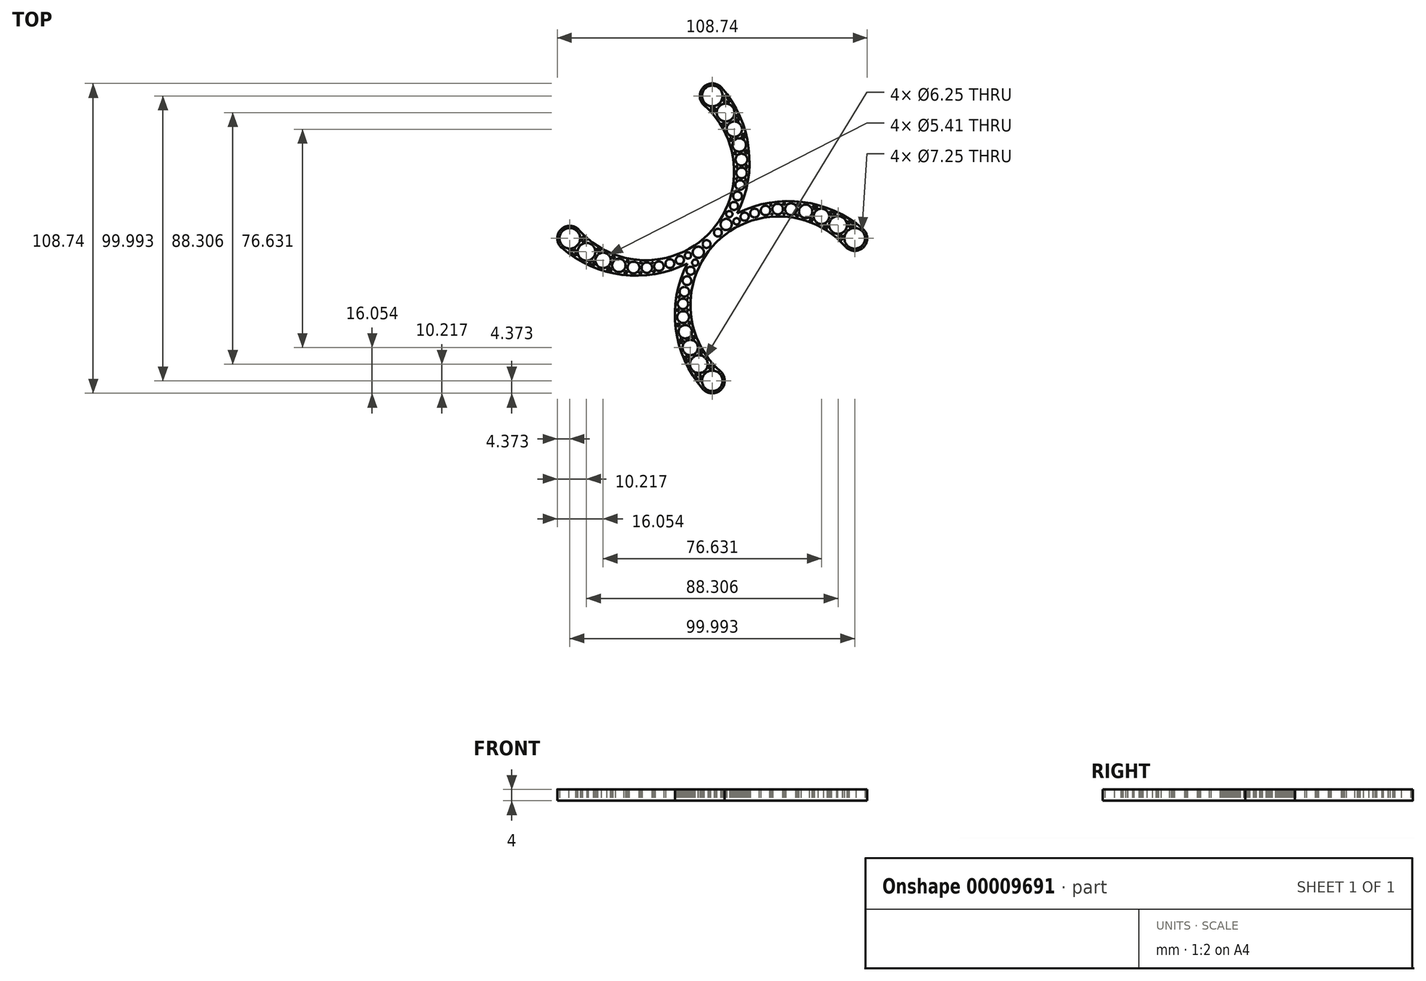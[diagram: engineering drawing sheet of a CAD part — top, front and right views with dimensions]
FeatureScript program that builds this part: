
annotation { "Feature Type Name" : "Feature", "Feature Type Description" : "" }
export const myFeature = defineFeature(function(context is Context, id is Id, definition is map)
    precondition{}
    {
        {
            var Q0;
            Q0=qCreatedBy(makeId("Top.planeOp"),FACE);
            var sketch = newSketch(context, id + "F0", { "sketchPlane" : qUnion([Q0])});
            skCircle(sketch, "E0.1.0", {"center": v(-50, 0) * mm, "radius": 3.62 * mm});
            skArc(sketch, "E0.1.1", {"start": v(-50.38, -4.36) * mm, "mid": v(-49.12, -4.29) * mm, "end": v(-47.93, -3.86) * mm});
            skArc(sketch, "E1", {"start": v(-46.7, 2.89) * mm, "mid": v(-24.38, -7.66) * mm, "end": v(-1.41, 1.41) * mm});
            skArc(sketch, "E2", {"start": v(-52.87, -3.3) * mm, "mid": v(-31.68, -12.77) * mm, "end": v(-8.81, -8.81) * mm});
            skArc(sketch, "E3.0", {"start": v(-50.38, -4.36) * mm, "mid": v(-49.07, -5.31) * mm, "end": v(-47.72, -6.21) * mm});
            skArc(sketch, "E4.0", {"start": v(-45.68, 0.7) * mm, "mid": v(-44.86, -0.08) * mm, "end": v(-44, -0.83) * mm});
            skPoint(sketch, "E5.orphan", {"position": v(-52.38, -2.74) * mm});
            skPoint(sketch, "E6.orphan", {"position": v(-47.27, 2.4) * mm});
            skArc(sketch, "E7.trimOffspring", {"start": v(-46.7, 2.89) * mm, "mid": v(-53.1, 3.09) * mm, "end": v(-52.87, -3.3) * mm});
            skArc(sketch, "E8", {"start": v(-47.93, -3.86) * mm, "mid": v(-48.01, -5.05) * mm, "end": v(-47.72, -6.21) * mm});
            skArc(sketch, "E9", {"start": v(-41.77, -7.75) * mm, "mid": v(-41.64, -8.67) * mm, "end": v(-41.27, -9.52) * mm});
            skCircle(sketch, "E10.0", {"center": v(-44.15, -4.7) * mm, "radius": 3.12 * mm});
            skCircle(sketch, "E11.0", {"center": v(-38.32, -7.73) * mm, "radius": 2.7 * mm});
            skArc(sketch, "E12", {"start": v(-33.98, -6.6) * mm, "mid": v(-34.47, -6.87) * mm, "end": v(-34.9, -7.2) * mm});
            skArc(sketch, "E13", {"start": v(-29.22, -7.89) * mm, "mid": v(-29.55, -8.15) * mm, "end": v(-29.84, -8.45) * mm});
            skArc(sketch, "E14", {"start": v(-24.77, -8.4) * mm, "mid": v(-24.98, -8.63) * mm, "end": v(-25.16, -8.89) * mm});
            skCircle(sketch, "E15.0", {"center": v(-32.77, -9.47) * mm, "radius": 2.36 * mm});
            skCircle(sketch, "E16.0", {"center": v(-27.65, -10.24) * mm, "radius": 2.08 * mm});
            skCircle(sketch, "E17.0", {"center": v(-22.97, -10.28) * mm, "radius": 1.85 * mm});
            skArc(sketch, "E18", {"start": v(-20.65, -8.31) * mm, "mid": v(-20.78, -8.5) * mm, "end": v(-20.9, -8.7) * mm});
            skCircle(sketch, "E19.0", {"center": v(-18.72, -9.78) * mm, "radius": 1.67 * mm});
            skCircle(sketch, "E20.0", {"center": v(-14.87, -8.86) * mm, "radius": 1.54 * mm});
            skCircle(sketch, "E21.0", {"center": v(-11.37, -7.62) * mm, "radius": 1.43 * mm});
            skCircle(sketch, "E22.0", {"center": v(-8.52, -5.99) * mm, "radius": 1.1 * mm});
            skCircle(sketch, "E23.0", {"center": v(-4.88, -4.88) * mm, "radius": 1.96 * mm});
            skCircle(sketch, "E24.0", {"center": v(-2, -2) * mm, "radius": 1.37 * mm});
            skArc(sketch, "E25.trimOffspring", {"start": v(-45.79, -1.19) * mm, "mid": v(-45.63, -0.25) * mm, "end": v(-45.68, 0.7) * mm});
            skArc(sketch, "E26.trimOffspring", {"start": v(-44, -0.83) * mm, "mid": v(-44.92, -0.9) * mm, "end": v(-45.79, -1.19) * mm});
            skArc(sketch, "E27.trimOffspring", {"start": v(-40.5, -3.43) * mm, "mid": v(-39.74, -3.9) * mm, "end": v(-38.97, -4.34) * mm});
            skArc(sketch, "E28.trimOffspring", {"start": v(-43.54, -8.53) * mm, "mid": v(-42.41, -9.04) * mm, "end": v(-41.27, -9.52) * mm});
            skArc(sketch, "E29.trimOffspring", {"start": v(-43.54, -8.53) * mm, "mid": v(-42.6, -8.25) * mm, "end": v(-41.77, -7.75) * mm});
            skArc(sketch, "E30.trimOffspring", {"start": v(-35.26, -6.13) * mm, "mid": v(-34.62, -6.37) * mm, "end": v(-33.98, -6.6) * mm});
            skArc(sketch, "E31.trimOffspring", {"start": v(-38.97, -4.34) * mm, "mid": v(-39.66, -4.55) * mm, "end": v(-40.28, -4.9) * mm});
            skArc(sketch, "E32.trimOffspring", {"start": v(-40.28, -4.9) * mm, "mid": v(-40.32, -4.15) * mm, "end": v(-40.5, -3.43) * mm});
            skArc(sketch, "E33.trimOffspring", {"start": v(-37.05, -10.94) * mm, "mid": v(-36.38, -10.6) * mm, "end": v(-35.81, -10.1) * mm});
            skArc(sketch, "E34.trimOffspring", {"start": v(-37.05, -10.94) * mm, "mid": v(-36.13, -11.18) * mm, "end": v(-35.2, -11.4) * mm});
            skArc(sketch, "E35.trimOffspring", {"start": v(-30.23, -7.68) * mm, "mid": v(-29.73, -7.79) * mm, "end": v(-29.22, -7.89) * mm});
            skArc(sketch, "E36.trimOffspring", {"start": v(-34.9, -7.2) * mm, "mid": v(-35.04, -6.65) * mm, "end": v(-35.26, -6.13) * mm});
            skArc(sketch, "E37.trimOffspring", {"start": v(-35.81, -10.1) * mm, "mid": v(-35.59, -10.79) * mm, "end": v(-35.2, -11.4) * mm});
            skArc(sketch, "E38.trimOffspring", {"start": v(-31.1, -12.08) * mm, "mid": v(-30.38, -12.16) * mm, "end": v(-29.66, -12.22) * mm});
            skArc(sketch, "E39.trimOffspring", {"start": v(-31.1, -12.08) * mm, "mid": v(-30.64, -11.73) * mm, "end": v(-30.26, -11.3) * mm});
            skArc(sketch, "E40.trimOffspring", {"start": v(-30.26, -11.3) * mm, "mid": v(-30, -11.79) * mm, "end": v(-29.66, -12.22) * mm});
            skArc(sketch, "E41.trimOffspring", {"start": v(-29.84, -8.45) * mm, "mid": v(-30, -8.05) * mm, "end": v(-30.23, -7.68) * mm});
            skArc(sketch, "E42.trimOffspring", {"start": v(-25.19, -11.64) * mm, "mid": v(-24.94, -11.97) * mm, "end": v(-24.65, -12.27) * mm});
            skArc(sketch, "E43.trimOffspring", {"start": v(-25.16, -8.89) * mm, "mid": v(-25.33, -8.61) * mm, "end": v(-25.53, -8.36) * mm});
            skArc(sketch, "E44.trimOffspring", {"start": v(-20.58, -11.33) * mm, "mid": v(-20.37, -11.56) * mm, "end": v(-20.12, -11.76) * mm});
            skArc(sketch, "E45.trimOffspring", {"start": v(-20.9, -8.7) * mm, "mid": v(-21.04, -8.53) * mm, "end": v(-21.21, -8.36) * mm});
            skArc(sketch, "E46.trimOffspring", {"start": v(-21.21, -8.36) * mm, "mid": v(-20.93, -8.34) * mm, "end": v(-20.65, -8.31) * mm});
            skArc(sketch, "E47.trimOffspring", {"start": v(-25.73, -12.31) * mm, "mid": v(-25.19, -12.3) * mm, "end": v(-24.65, -12.27) * mm});
            skArc(sketch, "E48.trimOffspring", {"start": v(-25.73, -12.31) * mm, "mid": v(-25.43, -12) * mm, "end": v(-25.19, -11.64) * mm});
            skArc(sketch, "E49.trimOffspring", {"start": v(-20.92, -11.89) * mm, "mid": v(-20.73, -11.62) * mm, "end": v(-20.58, -11.33) * mm});
            skArc(sketch, "E50.trimOffspring", {"start": v(-20.92, -11.89) * mm, "mid": v(-20.52, -11.83) * mm, "end": v(-20.12, -11.76) * mm});
            skLineSegment(sketch, "E51", {"start": v(-25.53, -8.36) * mm, "end": v(-24.77, -8.4) * mm});
            skArc(sketch, "E52.2.MirrorCS", {"start": v(-6.6, -33.98) * mm, "mid": v(-6.87, -34.47) * mm, "end": v(-7.2, -34.9) * mm});
            skArc(sketch, "E52.3.MirrorCS", {"start": v(-7.2, -34.9) * mm, "mid": v(-6.65, -35.04) * mm, "end": v(-6.13, -35.26) * mm});
            skCircle(sketch, "E52.4.MirrorC", {"center": v(-5.99, -8.52) * mm, "radius": 1.1 * mm});
            skArc(sketch, "E52.8.MirrorCS", {"start": v(-6.13, -35.26) * mm, "mid": v(-6.37, -34.62) * mm, "end": v(-6.6, -33.98) * mm});
            skArc(sketch, "E52.9.MirrorCS", {"start": v(-11.89, -20.92) * mm, "mid": v(-11.62, -20.73) * mm, "end": v(-11.33, -20.58) * mm});
            skArc(sketch, "E52.10.MirrorCS", {"start": v(-8.89, -25.16) * mm, "mid": v(-8.61, -25.33) * mm, "end": v(-8.36, -25.53) * mm});
            skArc(sketch, "E52.11.MirrorCS", {"start": v(-8.4, -24.77) * mm, "mid": v(-8.63, -24.98) * mm, "end": v(-8.89, -25.16) * mm});
            skLineSegment(sketch, "E52.13.MirrorCS", {"start": v(-8.36, -25.53) * mm, "end": v(-8.4, -24.77) * mm});
            skArc(sketch, "E52.14.MirrorCS", {"start": v(-8.31, -20.65) * mm, "mid": v(-8.5, -20.78) * mm, "end": v(-8.7, -20.9) * mm});
            skArc(sketch, "E52.18.MirrorCS", {"start": v(-10.1, -35.81) * mm, "mid": v(-10.79, -35.59) * mm, "end": v(-11.4, -35.2) * mm});
            skArc(sketch, "E52.19.MirrorCS", {"start": v(-10.94, -37.05) * mm, "mid": v(-10.6, -36.38) * mm, "end": v(-10.1, -35.81) * mm});
            skCircle(sketch, "E52.20.MirrorC", {"center": v(-7.62, -11.37) * mm, "radius": 1.43 * mm});
            skArc(sketch, "E52.21.MirrorCS", {"start": v(-10.94, -37.05) * mm, "mid": v(-11.18, -36.13) * mm, "end": v(-11.4, -35.2) * mm});
            skArc(sketch, "E52.22.MirrorCS", {"start": v(-4.36, -50.38) * mm, "mid": v(-5.31, -49.07) * mm, "end": v(-6.21, -47.72) * mm});
            skArc(sketch, "E52.23.MirrorCS", {"start": v(0.7, -45.68) * mm, "mid": v(-0.08, -44.86) * mm, "end": v(-0.83, -44) * mm});
            skArc(sketch, "E52.24.MirrorCS", {"start": v(-4.36, -50.38) * mm, "mid": v(-4.29, -49.12) * mm, "end": v(-3.86, -47.93) * mm});
            skArc(sketch, "E52.25.MirrorCS", {"start": v(-11.89, -20.92) * mm, "mid": v(-11.83, -20.52) * mm, "end": v(-11.76, -20.12) * mm});
            skArc(sketch, "E52.27.MirrorCS", {"start": v(-12.31, -25.73) * mm, "mid": v(-12, -25.43) * mm, "end": v(-11.64, -25.19) * mm});
            skArc(sketch, "E52.28.MirrorCS", {"start": v(-12.08, -31.1) * mm, "mid": v(-11.73, -30.64) * mm, "end": v(-11.3, -30.26) * mm});
            skCircle(sketch, "E52.29.MirrorC", {"center": v(-8.86, -14.87) * mm, "radius": 1.54 * mm});
            skArc(sketch, "E52.30.MirrorCS", {"start": v(-12.08, -31.1) * mm, "mid": v(-12.16, -30.38) * mm, "end": v(-12.22, -29.66) * mm});
            skArc(sketch, "E52.31.MirrorCS", {"start": v(-7.68, -30.23) * mm, "mid": v(-7.79, -29.73) * mm, "end": v(-7.89, -29.22) * mm});
            skArc(sketch, "E52.32.MirrorCS", {"start": v(-11.33, -20.58) * mm, "mid": v(-11.56, -20.37) * mm, "end": v(-11.76, -20.12) * mm});
            skArc(sketch, "E52.34.MirrorCS", {"start": v(-12.31, -25.73) * mm, "mid": v(-12.3, -25.19) * mm, "end": v(-12.27, -24.65) * mm});
            skArc(sketch, "E52.35.MirrorCS", {"start": v(-8.36, -21.21) * mm, "mid": v(-8.34, -20.93) * mm, "end": v(-8.31, -20.65) * mm});
            skArc(sketch, "E52.37.MirrorCS", {"start": v(-11.3, -30.26) * mm, "mid": v(-11.79, -30) * mm, "end": v(-12.22, -29.66) * mm});
            skArc(sketch, "E52.38.MirrorCS", {"start": v(-3.86, -47.93) * mm, "mid": v(-5.05, -48.01) * mm, "end": v(-6.21, -47.72) * mm});
            skArc(sketch, "E52.41.MirrorCS", {"start": v(-1.19, -45.79) * mm, "mid": v(-0.25, -45.63) * mm, "end": v(0.7, -45.68) * mm});
            skArc(sketch, "E52.42.MirrorCS", {"start": v(-8.45, -29.84) * mm, "mid": v(-8.05, -30) * mm, "end": v(-7.68, -30.23) * mm});
            skArc(sketch, "E52.43.MirrorCS", {"start": v(-7.89, -29.22) * mm, "mid": v(-8.15, -29.55) * mm, "end": v(-8.45, -29.84) * mm});
            skArc(sketch, "E52.44.MirrorCS", {"start": v(-11.64, -25.19) * mm, "mid": v(-11.97, -24.94) * mm, "end": v(-12.27, -24.65) * mm});
            skArc(sketch, "E52.47.MirrorCS", {"start": v(-8.7, -20.9) * mm, "mid": v(-8.53, -21.04) * mm, "end": v(-8.36, -21.21) * mm});
            skArc(sketch, "E52.48.MirrorCS", {"start": v(-4.9, -40.28) * mm, "mid": v(-4.15, -40.32) * mm, "end": v(-3.43, -40.5) * mm});
            skArc(sketch, "E52.49.MirrorCS", {"start": v(-7.75, -41.77) * mm, "mid": v(-8.67, -41.64) * mm, "end": v(-9.52, -41.27) * mm});
            skArc(sketch, "E52.50.MirrorCS", {"start": v(-8.53, -43.54) * mm, "mid": v(-9.04, -42.41) * mm, "end": v(-9.52, -41.27) * mm});
            skArc(sketch, "E52.51.MirrorCS", {"start": v(-4.34, -38.97) * mm, "mid": v(-4.55, -39.66) * mm, "end": v(-4.9, -40.28) * mm});
            skArc(sketch, "E52.52.MirrorCS", {"start": v(-3.43, -40.5) * mm, "mid": v(-3.9, -39.74) * mm, "end": v(-4.34, -38.97) * mm});
            skArc(sketch, "E52.53.MirrorCS", {"start": v(-0.83, -44) * mm, "mid": v(-0.9, -44.92) * mm, "end": v(-1.19, -45.79) * mm});
            skArc(sketch, "E52.54.MirrorCS", {"start": v(-8.53, -43.54) * mm, "mid": v(-8.25, -42.6) * mm, "end": v(-7.75, -41.77) * mm});
            skPoint(sketch, "E52.55.MirrorP", {"position": v(2.4, -47.27) * mm});
            skArc(sketch, "E52.56.MirrorCS", {"start": v(-3.3, -52.87) * mm, "mid": v(-12.77, -31.68) * mm, "end": v(-8.81, -8.81) * mm});
            skCircle(sketch, "E52.57.MirrorC", {"center": v(0, -50) * mm, "radius": 3.62 * mm});
            skCircle(sketch, "E52.58.MirrorC", {"center": v(-7.73, -38.32) * mm, "radius": 2.7 * mm});
            skCircle(sketch, "E52.59.MirrorC", {"center": v(-10.28, -22.97) * mm, "radius": 1.85 * mm});
            skArc(sketch, "E52.60.MirrorCS", {"start": v(2.89, -46.7) * mm, "mid": v(3.09, -53.1) * mm, "end": v(-3.3, -52.87) * mm});
            skCircle(sketch, "E52.61.MirrorC", {"center": v(-9.78, -18.72) * mm, "radius": 1.67 * mm});
            skCircle(sketch, "E52.62.MirrorC", {"center": v(-4.7, -44.15) * mm, "radius": 3.12 * mm});
            skCircle(sketch, "E52.63.MirrorC", {"center": v(-9.47, -32.77) * mm, "radius": 2.36 * mm});
            skCircle(sketch, "E52.64.MirrorC", {"center": v(-10.24, -27.65) * mm, "radius": 2.08 * mm});
            skPoint(sketch, "E52.65.MirrorP", {"position": v(-2.74, -52.38) * mm});
            skArc(sketch, "E53.0.MirrorCS", {"start": v(2.89, -46.7) * mm, "mid": v(-7.66, -24.38) * mm, "end": v(1.41, -1.41) * mm});
            skLineSegment(sketch, "E54.11.MirrorCS", {"start": v(8.36, 25.53) * mm, "end": v(8.4, 24.77) * mm});
            skCircle(sketch, "E54.13.MirrorC", {"center": v(5.99, 8.52) * mm, "radius": 1.1 * mm});
            skCircle(sketch, "E54.15.MirrorC", {"center": v(7.62, 11.37) * mm, "radius": 1.43 * mm});
            skArc(sketch, "E54.20.MirrorCS", {"start": v(8.36, 21.21) * mm, "mid": v(8.34, 20.93) * mm, "end": v(8.31, 20.65) * mm});
            skArc(sketch, "E54.21.MirrorCS", {"start": v(20.65, 8.31) * mm, "mid": v(20.78, 8.5) * mm, "end": v(20.9, 8.7) * mm});
            skArc(sketch, "E54.22.MirrorCS", {"start": v(25.19, 11.64) * mm, "mid": v(24.94, 11.97) * mm, "end": v(24.65, 12.27) * mm});
            skArc(sketch, "E54.23.MirrorCS", {"start": v(8.4, 24.77) * mm, "mid": v(8.63, 24.98) * mm, "end": v(8.89, 25.16) * mm});
            skArc(sketch, "E54.25.MirrorCS", {"start": v(11.33, 20.58) * mm, "mid": v(11.56, 20.37) * mm, "end": v(11.76, 20.12) * mm});
            skArc(sketch, "E54.27.MirrorCS", {"start": v(12.31, 25.73) * mm, "mid": v(12, 25.43) * mm, "end": v(11.64, 25.19) * mm});
            skArc(sketch, "E54.31.MirrorCS", {"start": v(8.89, 25.16) * mm, "mid": v(8.61, 25.33) * mm, "end": v(8.36, 25.53) * mm});
            skArc(sketch, "E54.33.MirrorCS", {"start": v(8.7, 20.9) * mm, "mid": v(8.53, 21.04) * mm, "end": v(8.36, 21.21) * mm});
            skArc(sketch, "E54.34.MirrorCS", {"start": v(12.31, 25.73) * mm, "mid": v(12.3, 25.19) * mm, "end": v(12.27, 24.65) * mm});
            skArc(sketch, "E54.35.MirrorCS", {"start": v(20.9, 8.7) * mm, "mid": v(21.04, 8.53) * mm, "end": v(21.21, 8.36) * mm});
            skArc(sketch, "E54.36.MirrorCS", {"start": v(30.23, 7.68) * mm, "mid": v(29.73, 7.79) * mm, "end": v(29.22, 7.89) * mm});
            skArc(sketch, "E54.37.MirrorCS", {"start": v(7.68, 30.23) * mm, "mid": v(7.79, 29.73) * mm, "end": v(7.89, 29.22) * mm});
            skArc(sketch, "E54.38.MirrorCS", {"start": v(8.31, 20.65) * mm, "mid": v(8.5, 20.78) * mm, "end": v(8.7, 20.9) * mm});
            skArc(sketch, "E54.41.MirrorCS", {"start": v(11.64, 25.19) * mm, "mid": v(11.97, 24.94) * mm, "end": v(12.27, 24.65) * mm});
            skCircle(sketch, "E54.42.MirrorC", {"center": v(14.87, 8.86) * mm, "radius": 1.54 * mm});
            skCircle(sketch, "E54.44.MirrorC", {"center": v(8.52, 5.99) * mm, "radius": 1.1 * mm});
            skArc(sketch, "E54.47.MirrorCS", {"start": v(10.1, 35.81) * mm, "mid": v(10.79, 35.59) * mm, "end": v(11.4, 35.2) * mm});
            skArc(sketch, "E54.48.MirrorCS", {"start": v(4.36, 50.38) * mm, "mid": v(4.29, 49.12) * mm, "end": v(3.86, 47.93) * mm});
            skArc(sketch, "E54.49.MirrorCS", {"start": v(10.94, 37.05) * mm, "mid": v(11.18, 36.13) * mm, "end": v(11.4, 35.2) * mm});
            skArc(sketch, "E54.50.MirrorCS", {"start": v(29.84, 8.45) * mm, "mid": v(30, 8.05) * mm, "end": v(30.23, 7.68) * mm});
            skArc(sketch, "E54.51.MirrorCS", {"start": v(31.1, 12.08) * mm, "mid": v(30.38, 12.16) * mm, "end": v(29.66, 12.22) * mm});
            skCircle(sketch, "E54.53.MirrorC", {"center": v(18.72, 9.78) * mm, "radius": 1.67 * mm});
            skArc(sketch, "E54.54.MirrorCS", {"start": v(-0.7, 45.68) * mm, "mid": v(0.08, 44.86) * mm, "end": v(0.83, 44) * mm});
            skArc(sketch, "E54.55.MirrorCS", {"start": v(4.36, 50.38) * mm, "mid": v(5.31, 49.07) * mm, "end": v(6.21, 47.72) * mm});
            skArc(sketch, "E54.56.MirrorCS", {"start": v(3.86, 47.93) * mm, "mid": v(5.05, 48.01) * mm, "end": v(6.21, 47.72) * mm});
            skArc(sketch, "E54.57.MirrorCS", {"start": v(7.89, 29.22) * mm, "mid": v(8.15, 29.55) * mm, "end": v(8.45, 29.84) * mm});
            skArc(sketch, "E54.59.MirrorCS", {"start": v(6.13, 35.26) * mm, "mid": v(6.37, 34.62) * mm, "end": v(6.6, 33.98) * mm});
            skArc(sketch, "E54.62.MirrorCS", {"start": v(11.89, 20.92) * mm, "mid": v(11.62, 20.73) * mm, "end": v(11.33, 20.58) * mm});
            skArc(sketch, "E54.63.MirrorCS", {"start": v(35.26, 6.13) * mm, "mid": v(34.62, 6.37) * mm, "end": v(33.98, 6.6) * mm});
            skArc(sketch, "E54.64.MirrorCS", {"start": v(25.73, 12.31) * mm, "mid": v(25.43, 12) * mm, "end": v(25.19, 11.64) * mm});
            skArc(sketch, "E54.65.MirrorCS", {"start": v(10.94, 37.05) * mm, "mid": v(10.6, 36.38) * mm, "end": v(10.1, 35.81) * mm});
            skArc(sketch, "E54.66.MirrorCS", {"start": v(29.22, 7.89) * mm, "mid": v(29.55, 8.15) * mm, "end": v(29.84, 8.45) * mm});
            skArc(sketch, "E54.67.MirrorCS", {"start": v(6.6, 33.98) * mm, "mid": v(6.87, 34.47) * mm, "end": v(7.2, 34.9) * mm});
            skCircle(sketch, "E54.68.MirrorC", {"center": v(4.88, 4.88) * mm, "radius": 1.96 * mm});
            skArc(sketch, "E54.69.MirrorCS", {"start": v(7.2, 34.9) * mm, "mid": v(6.65, 35.04) * mm, "end": v(6.13, 35.26) * mm});
            skArc(sketch, "E54.70.MirrorCS", {"start": v(20.58, 11.33) * mm, "mid": v(20.37, 11.56) * mm, "end": v(20.12, 11.76) * mm});
            skArc(sketch, "E54.71.MirrorCS", {"start": v(34.9, 7.2) * mm, "mid": v(35.04, 6.65) * mm, "end": v(35.26, 6.13) * mm});
            skArc(sketch, "E54.72.MirrorCS", {"start": v(40.28, 4.9) * mm, "mid": v(40.32, 4.15) * mm, "end": v(40.5, 3.43) * mm});
            skArc(sketch, "E54.73.MirrorCS", {"start": v(4.9, 40.28) * mm, "mid": v(4.15, 40.32) * mm, "end": v(3.43, 40.5) * mm});
            skCircle(sketch, "E54.74.MirrorC", {"center": v(8.86, 14.87) * mm, "radius": 1.54 * mm});
            skArc(sketch, "E54.76.MirrorCS", {"start": v(38.97, 4.34) * mm, "mid": v(39.66, 4.55) * mm, "end": v(40.28, 4.9) * mm});
            skArc(sketch, "E54.77.MirrorCS", {"start": v(21.21, 8.36) * mm, "mid": v(20.93, 8.34) * mm, "end": v(20.65, 8.31) * mm});
            skArc(sketch, "E54.78.MirrorCS", {"start": v(1.19, 45.79) * mm, "mid": v(0.25, 45.63) * mm, "end": v(-0.7, 45.68) * mm});
            skArc(sketch, "E54.80.MirrorCS", {"start": v(25.73, 12.31) * mm, "mid": v(25.19, 12.3) * mm, "end": v(24.65, 12.27) * mm});
            skArc(sketch, "E54.81.MirrorCS", {"start": v(33.98, 6.6) * mm, "mid": v(34.47, 6.87) * mm, "end": v(34.9, 7.2) * mm});
            skArc(sketch, "E54.82.MirrorCS", {"start": v(45.68, -0.7) * mm, "mid": v(44.86, 0.08) * mm, "end": v(44, 0.83) * mm});
            skArc(sketch, "E54.83.MirrorCS", {"start": v(20.92, 11.89) * mm, "mid": v(20.73, 11.62) * mm, "end": v(20.58, 11.33) * mm});
            skArc(sketch, "E54.84.MirrorCS", {"start": v(20.92, 11.89) * mm, "mid": v(20.52, 11.83) * mm, "end": v(20.12, 11.76) * mm});
            skArc(sketch, "E54.85.MirrorCS", {"start": v(45.79, 1.19) * mm, "mid": v(45.63, 0.25) * mm, "end": v(45.68, -0.7) * mm});
            skArc(sketch, "E54.86.MirrorCS", {"start": v(12.08, 31.1) * mm, "mid": v(11.73, 30.64) * mm, "end": v(11.3, 30.26) * mm});
            skCircle(sketch, "E54.89.MirrorC", {"center": v(11.37, 7.62) * mm, "radius": 1.43 * mm});
            skArc(sketch, "E54.90.MirrorCS", {"start": v(4.34, 38.97) * mm, "mid": v(4.55, 39.66) * mm, "end": v(4.9, 40.28) * mm});
            skCircle(sketch, "E54.91.MirrorC", {"center": v(9.78, 18.72) * mm, "radius": 1.67 * mm});
            skArc(sketch, "E54.92.MirrorCS", {"start": v(25.16, 8.89) * mm, "mid": v(25.33, 8.61) * mm, "end": v(25.53, 8.36) * mm});
            skArc(sketch, "E54.93.MirrorCS", {"start": v(11.89, 20.92) * mm, "mid": v(11.83, 20.52) * mm, "end": v(11.76, 20.12) * mm});
            skArc(sketch, "E54.94.MirrorCS", {"start": v(8.45, 29.84) * mm, "mid": v(8.05, 30) * mm, "end": v(7.68, 30.23) * mm});
            skArc(sketch, "E54.95.MirrorCS", {"start": v(3.43, 40.5) * mm, "mid": v(3.9, 39.74) * mm, "end": v(4.34, 38.97) * mm});
            skCircle(sketch, "E54.96.MirrorC", {"center": v(7.73, 38.32) * mm, "radius": 2.7 * mm});
            skArc(sketch, "E54.97.MirrorCS", {"start": v(44, 0.83) * mm, "mid": v(44.92, 0.9) * mm, "end": v(45.79, 1.19) * mm});
            skArc(sketch, "E54.98.MirrorCS", {"start": v(37.05, 10.94) * mm, "mid": v(36.13, 11.18) * mm, "end": v(35.2, 11.4) * mm});
            skArc(sketch, "E54.99.MirrorCS", {"start": v(30.26, 11.3) * mm, "mid": v(30, 11.79) * mm, "end": v(29.66, 12.22) * mm});
            skArc(sketch, "E54.100.MirrorCS", {"start": v(12.08, 31.1) * mm, "mid": v(12.16, 30.38) * mm, "end": v(12.22, 29.66) * mm});
            skArc(sketch, "E54.101.MirrorCS", {"start": v(43.54, 8.53) * mm, "mid": v(42.6, 8.25) * mm, "end": v(41.77, 7.75) * mm});
            skCircle(sketch, "E54.102.MirrorC", {"center": v(4.7, 44.15) * mm, "radius": 3.12 * mm});
            skCircle(sketch, "E54.103.MirrorC", {"center": v(9.47, 32.77) * mm, "radius": 2.36 * mm});
            skArc(sketch, "E54.104.MirrorCS", {"start": v(40.5, 3.43) * mm, "mid": v(39.74, 3.9) * mm, "end": v(38.97, 4.34) * mm});
            skArc(sketch, "E54.105.MirrorCS", {"start": v(41.77, 7.75) * mm, "mid": v(41.64, 8.67) * mm, "end": v(41.27, 9.52) * mm});
            skArc(sketch, "E54.106.MirrorCS", {"start": v(50.38, 4.36) * mm, "mid": v(49.12, 4.29) * mm, "end": v(47.93, 3.86) * mm});
            skArc(sketch, "E54.107.MirrorCS", {"start": v(7.75, 41.77) * mm, "mid": v(8.67, 41.64) * mm, "end": v(9.52, 41.27) * mm});
            skArc(sketch, "E54.108.MirrorCS", {"start": v(47.93, 3.86) * mm, "mid": v(48.01, 5.05) * mm, "end": v(47.72, 6.21) * mm});
            skCircle(sketch, "E54.109.MirrorC", {"center": v(22.97, 10.28) * mm, "radius": 1.85 * mm});
            skCircle(sketch, "E54.110.MirrorC", {"center": v(2, 2) * mm, "radius": 1.37 * mm});
            skLineSegment(sketch, "E54.111.MirrorCS", {"start": v(25.53, 8.36) * mm, "end": v(24.77, 8.4) * mm});
            skArc(sketch, "E54.112.MirrorCS", {"start": v(37.05, 10.94) * mm, "mid": v(36.38, 10.6) * mm, "end": v(35.81, 10.1) * mm});
            skArc(sketch, "E54.113.MirrorCS", {"start": v(8.53, 43.54) * mm, "mid": v(8.25, 42.6) * mm, "end": v(7.75, 41.77) * mm});
            skArc(sketch, "E54.114.MirrorCS", {"start": v(35.81, 10.1) * mm, "mid": v(35.59, 10.79) * mm, "end": v(35.2, 11.4) * mm});
            skArc(sketch, "E54.115.MirrorCS", {"start": v(43.54, 8.53) * mm, "mid": v(42.41, 9.04) * mm, "end": v(41.27, 9.52) * mm});
            skArc(sketch, "E54.116.MirrorCS", {"start": v(50.38, 4.36) * mm, "mid": v(49.07, 5.31) * mm, "end": v(47.72, 6.21) * mm});
            skArc(sketch, "E54.117.MirrorCS", {"start": v(31.1, 12.08) * mm, "mid": v(30.64, 11.73) * mm, "end": v(30.26, 11.3) * mm});
            skCircle(sketch, "E54.118.MirrorC", {"center": v(10.24, 27.65) * mm, "radius": 2.08 * mm});
            skArc(sketch, "E54.119.MirrorCS", {"start": v(0.83, 44) * mm, "mid": v(0.9, 44.92) * mm, "end": v(1.19, 45.79) * mm});
            skArc(sketch, "E54.120.MirrorCS", {"start": v(8.53, 43.54) * mm, "mid": v(9.04, 42.41) * mm, "end": v(9.52, 41.27) * mm});
            skCircle(sketch, "E54.121.MirrorC", {"center": v(10.28, 22.97) * mm, "radius": 1.85 * mm});
            skArc(sketch, "E54.122.MirrorCS", {"start": v(24.77, 8.4) * mm, "mid": v(24.98, 8.63) * mm, "end": v(25.16, 8.89) * mm});
            skCircle(sketch, "E54.123.MirrorC", {"center": v(0, 50) * mm, "radius": 3.62 * mm});
            skArc(sketch, "E54.124.MirrorCS", {"start": v(3.3, 52.87) * mm, "mid": v(12.77, 31.68) * mm, "end": v(8.81, 8.81) * mm});
            skArc(sketch, "E54.125.MirrorCS", {"start": v(-2.89, 46.7) * mm, "mid": v(7.66, 24.38) * mm, "end": v(-1.41, 1.41) * mm});
            skArc(sketch, "E54.126.MirrorCS", {"start": v(-2.89, 46.7) * mm, "mid": v(-3.09, 53.1) * mm, "end": v(3.3, 52.87) * mm});
            skCircle(sketch, "E54.127.MirrorC", {"center": v(50, 0) * mm, "radius": 3.62 * mm});
            skPoint(sketch, "E54.128.MirrorP", {"position": v(2.74, 52.38) * mm});
            skPoint(sketch, "E54.129.MirrorP", {"position": v(47.27, -2.4) * mm});
            skArc(sketch, "E54.130.MirrorCS", {"start": v(46.7, -2.89) * mm, "mid": v(24.38, 7.66) * mm, "end": v(1.41, -1.41) * mm});
            skPoint(sketch, "E54.131.MirrorP", {"position": v(-2.4, 47.27) * mm});
            skArc(sketch, "E54.132.MirrorCS", {"start": v(52.87, 3.3) * mm, "mid": v(31.68, 12.77) * mm, "end": v(8.81, 8.81) * mm});
            skCircle(sketch, "E54.133.MirrorC", {"center": v(27.65, 10.24) * mm, "radius": 2.08 * mm});
            skCircle(sketch, "E54.134.MirrorC", {"center": v(38.32, 7.73) * mm, "radius": 2.7 * mm});
            skPoint(sketch, "E54.135.MirrorP", {"position": v(52.38, 2.74) * mm});
            skCircle(sketch, "E54.136.MirrorC", {"center": v(44.15, 4.7) * mm, "radius": 3.12 * mm});
            skCircle(sketch, "E54.137.MirrorC", {"center": v(32.77, 9.47) * mm, "radius": 2.36 * mm});
            skArc(sketch, "E54.138.MirrorCS", {"start": v(46.7, -2.89) * mm, "mid": v(53.1, -3.09) * mm, "end": v(52.87, 3.3) * mm});
            skArc(sketch, "E54.139.MirrorCS", {"start": v(11.3, 30.26) * mm, "mid": v(11.79, 30) * mm, "end": v(12.22, 29.66) * mm});
            skSolve(sketch);
        }
        {
            var Q0;
            Q0 = qSketchRegion(id + "F0", true);
            extrude(context, id + "F1", {"entities" : qUnion([Q0]), "depth" : 4 * mm});
        }
    });
